# Revit family: Bath-Alcove-KOHLER-Entity-K-26109
name_source: partatom
category: Plumbing Fixtures
revit_build: Autodesk Revit 2017 (Build: 20160225_1515(x64)
units: mm (PartAtom-declared; Revit-internal decimal feet)

## family parameters
Cut with Voids When Loaded = No
Host = Face
OmniClass Number = 23.31.15.00
OmniClass Title = Bathtubs
Part Type = Normal
Room Calculation Point = No
Round Connector Dimension = Use Diameter
Shared = No

## types (2) — shared parameters
ADA Compliant = No
Assembly Code = D2010500
CW Connection = No
Cold Water Inlet = Cold Water Inlet
Date Modified = 02/17/2020
Default Elevation = 0"
Drain Included = No
Finish = KOHLER-Acrylic-0-White
HW Connection = No
Height = 15 3/4"
Hot Water Inlet = Hot Water Inlet
Length = 60"
Manufacturer = KOHLER Co.
MasterFormat 1995 = 15410
MasterFormat 2004 = 22.41.19
Material = Acrylic
Product Documentation Link = https://www.us.kohler.com
Product Name = Entity
Product Page URL = http://www.us.kohler.com
URL = https://www.us.kohler.com
Vent Connection = No
Waste Connection = Yes
Waste Water Outlet = Waste Water Outlet
WaterSense Certified = No
Width = 30 1/4"

## per-type parameters (varying)
| type | Description | Drain | Model | Type |
| LA- Left-hand drain, 0-White | 60 inch x 30 inch alcove bath with integral apron, integral flange and left-hand drain | 7 5/16" | K-26109-LA-0 | 1 |
| RA- Right-hand drain, 0-White | 60 inch x 30 inch alcove bath with integral apron, integral flange and right-hand drain | 52 11/16" | K-26109-RA-0 | 2 |

## geometry (parser evidence)
native form markers: Sweep x5
no freeform markers — native parametric forms only
